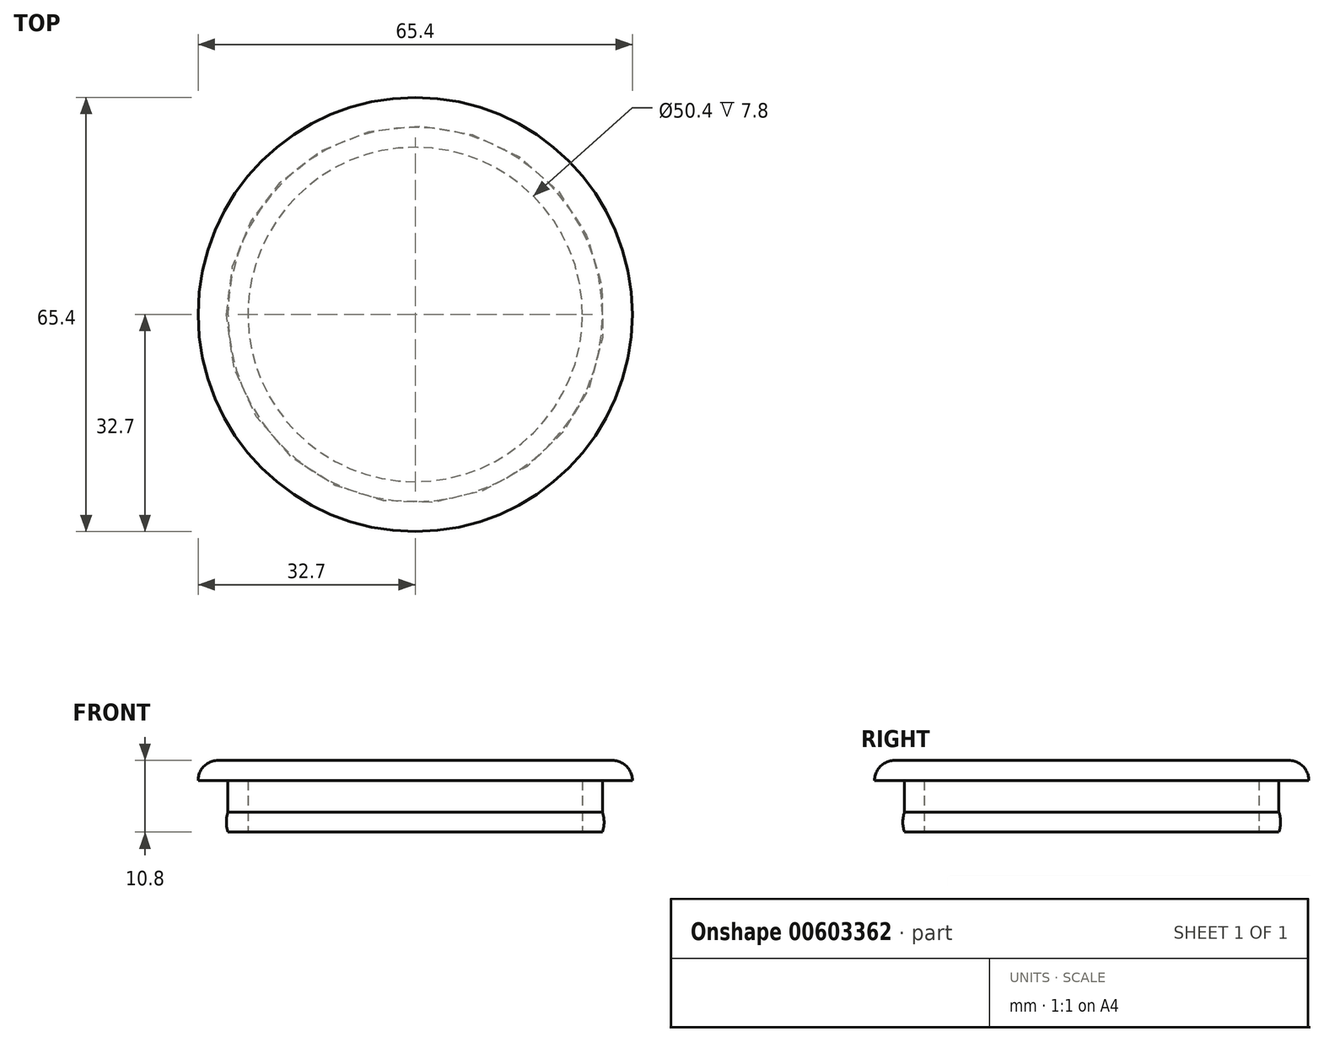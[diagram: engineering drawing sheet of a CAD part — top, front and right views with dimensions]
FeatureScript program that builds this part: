
annotation { "Feature Type Name" : "Feature", "Feature Type Description" : "" }
export const myFeature = defineFeature(function(context is Context, id is Id, definition is map)
    precondition{}
    {
        {
            var Q0;
            Q0=qCreatedBy(makeId("Front.planeOp"),FACE);
            var sketch = newSketch(context, id + "F0", { "sketchPlane" : qUnion([Q0])});
            skLineSegment(sketch, "E0.top", {"start": v(-25.2, -7.8) * mm, "end": v(-28.2, -7.8) * mm});
            skLineSegment(sketch, "E0.left", {"start": v(0, 0) * mm, "end": v(0, -7.8) * mm});
            skLineSegment(sketch, "E0.right", {"start": v(-28.2, 0) * mm, "end": v(-28.2, -4.8) * mm});
            skLineSegment(sketch, "E1.0", {"start": v(-25.2, 0) * mm, "end": v(-25.2, -7.8) * mm});
            skArc(sketch, "E2", {"start": v(-28.2, -4.8) * mm, "mid": v(-28.45, -6.3) * mm, "end": v(-28.2, -7.8) * mm});
            skLineSegment(sketch, "E3.bottom", {"start": v(-28.2, 0) * mm, "end": v(-32.7, 0) * mm});
            skLineSegment(sketch, "E3.top", {"start": v(0, 3) * mm, "end": v(-29.7, 3) * mm});
            skLineSegment(sketch, "E3.left", {"start": v(0, 0) * mm, "end": v(0, 3) * mm});
            skLineSegment(sketch, "E3.right", {"start": v(-32.7, 0) * mm, "end": v(-32.7, 0) * mm});
            skPoint(sketch, "E4.visualSharp", {"position": v(-32.7, 3) * mm});
            skArc(sketch, "E4.filletArc", {"start": v(-29.7, 3) * mm, "mid": v(-31.83, 2.12) * mm, "end": v(-32.7, 0) * mm});
            skLineSegment(sketch, "E5", {"start": v(-25.2, 0) * mm, "end": v(0, 0) * mm});
            skSolve(sketch);
        }
        {
            var Q0;
            Q0=makeQuery(id+"F0.imprint","IMPRINT",FACE,{"disambiguationData":[TD([[makeQuery(id+"F0.imprint","IMPRINT",EDGE,{"derivedFrom":sQuery(id+"F0.wireOp",EDGE,"E0.top")}),-1.0]])]});
            var Q1;
            Q1=sQuery(id+"F0.wireOp",EDGE,"E3.left");
            revolve(context, id + "F1", {"entities" : qUnion([Q0]), "axis" : qUnion([Q1]), "revolveType" : RevolveType.FULL});
        }
    });
